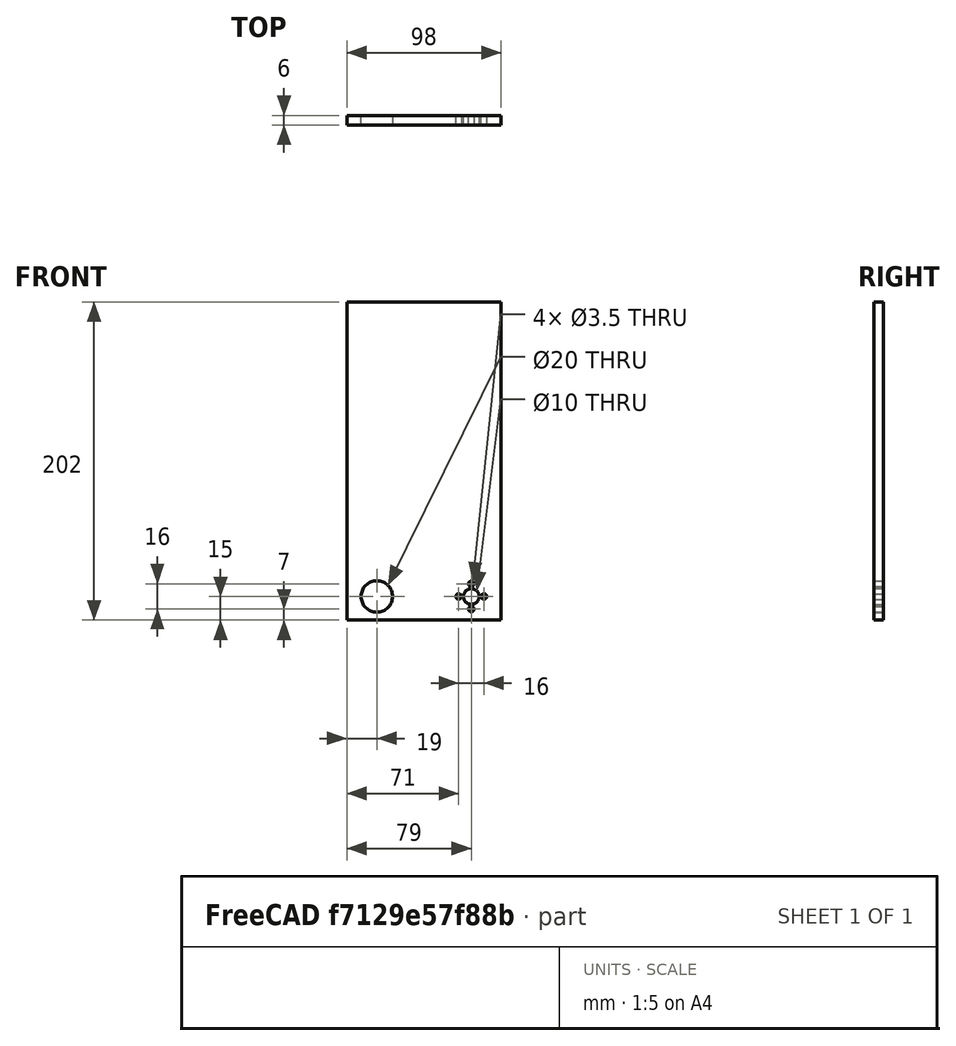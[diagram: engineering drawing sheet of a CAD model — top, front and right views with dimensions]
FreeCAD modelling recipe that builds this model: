
FCSTD DOCUMENT  (FreeCAD 0.18R4 (GitTag))
Label: Pusher1
License: All rights reserved
LicenseURL: http://en.wikipedia.org/wiki/All_rights_reserved
objects: Sketcher::SketchObject×1, PartDesign::Pad×1, PartDesign::Body×1
note: 4 computed .brp shape members not serialized (recipe doc carries the construction recipe); baked Part::Feature solids carry a one-line shape summary decoded from their .brp

FEATURE [Sketcher::SketchObject] Sketch
  MapMode = 5
  Placement = pos=(0,0,0) rot=(1,0,0;1.5708rad)
  Support = -> [XZ_Plane]
  sketch-geometry (10):
    g0: LineSegment StartX=0 StartY=0 StartZ=0 EndX=98 EndY=0 EndZ=0
    g1: LineSegment StartX=98 StartY=0 StartZ=0 EndX=98 EndY=202 EndZ=0
    g2: LineSegment StartX=0 StartY=202 StartZ=0 EndX=0 EndY=0 EndZ=0
    g3: Circle CenterX=19 CenterY=15 CenterZ=0 NormalX=0 NormalY=0 NormalZ=1 AngleXU=0 Radius=10
    g4: Circle CenterX=79 CenterY=15 CenterZ=0 NormalX=0 NormalY=0 NormalZ=1 AngleXU=0 Radius=5
    g5: Circle CenterX=79 CenterY=23 CenterZ=0 NormalX=0 NormalY=0 NormalZ=1 AngleXU=0 Radius=1.75
    g6: Circle CenterX=71 CenterY=15 CenterZ=0 NormalX=0 NormalY=0 NormalZ=1 AngleXU=0 Radius=1.75
    g7: Circle CenterX=79 CenterY=7 CenterZ=0 NormalX=0 NormalY=0 NormalZ=1 AngleXU=0 Radius=1.75
    g8: Circle CenterX=87 CenterY=15 CenterZ=0 NormalX=0 NormalY=0 NormalZ=1 AngleXU=0 Radius=1.75
    g9: LineSegment StartX=0 StartY=202 StartZ=0 EndX=98 EndY=202 EndZ=0
  constraints (29):
    c: Coincident(g0,g1)
    c: Coincident(g2,g0)
    c: Horizontal(g0)
    c: Vertical(g1)
    c: Vertical(g2)
    c: Coincident(g0,g-1)
    c: DistanceX(g0,g0) = 98
    c: DistanceY(g2,g2) = 202
    c: Radius(g3) = 10
    c: DistanceX(g3,g4) = 60
    c: Radius(g4) = 5
    c: Equal(g6,g7)
    c: Equal(g7,g5)
    c: Equal(g5,g8)
    c: Radius(g6) = 1.75
    c: DistanceY(g4,g5) = 8
    c: DistanceY(g7,g4) = 8
    c: DistanceX(g6,g4) = 8
    c: DistanceX(g4,g7) = 0
    c: DistanceX(g5,g7) = 0
    c: DistanceX(g4,g8) = 8
    c: DistanceY(g4,g8) = 0
    c: DistanceY(g6,g8) = 0
    c: Coincident(g2,g9)
    c: Coincident(g1,g9)
    c: Distance(g3,g0) = 15
    c: DistanceY(g3,g4) = 0
    c: Distance(g3,g2) = 19
    c: Horizontal(g9)
FEATURE [PartDesign::Pad] Pad
  Length = 6
  Length2 = 100
  Placement = pos=(0,0,0) rot=(1,0,0;1.5708rad)
  Profile = -> Sketch
  Type = 0
FEATURE [PartDesign::Body] Body
  Group = -> [Sketch,Pad]
  Origin = -> Origin
  Tip = -> Pad
